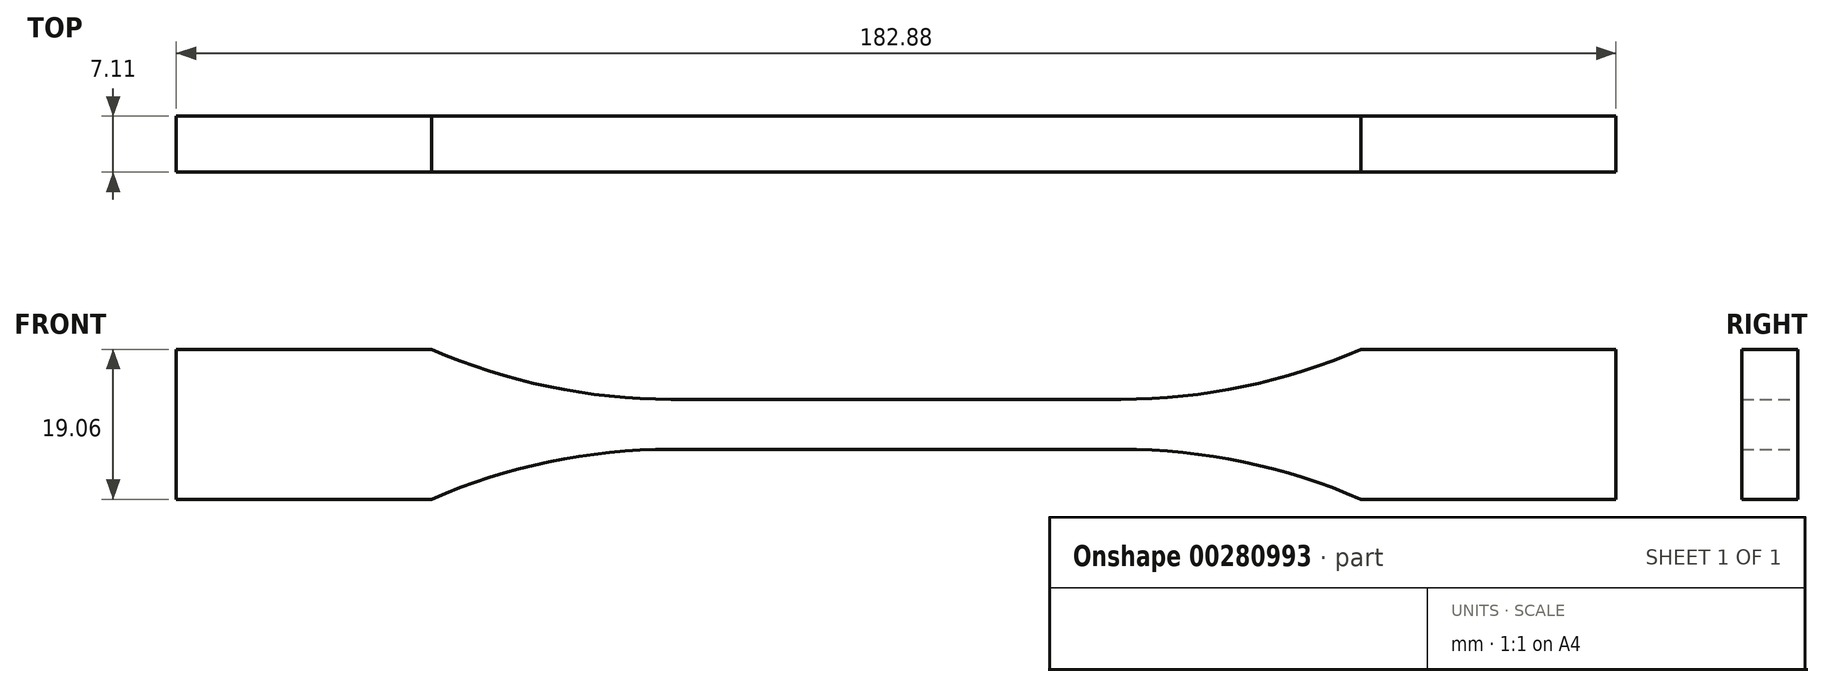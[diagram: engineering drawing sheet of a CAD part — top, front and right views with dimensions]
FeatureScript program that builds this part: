
annotation { "Feature Type Name" : "Feature", "Feature Type Description" : "" }
export const myFeature = defineFeature(function(context is Context, id is Id, definition is map)
    precondition{}
    {
        {
            var Q0;
            Q0=qCreatedBy(makeId("Front.planeOp"),FACE);
            var sketch = newSketch(context, id + "F0", { "sketchPlane" : qUnion([Q0])});
            skLineSegment(sketch, "E0", {"start": v(0, 3.17) * mm, "end": v(28.58, 3.17) * mm});
            skArc(sketch, "E1", {"start": v(28.58, 3.18) * mm, "mid": v(44.13, 4.78) * mm, "end": v(59.03, 9.52) * mm});
            skLineSegment(sketch, "E2", {"start": v(59.03, 9.53) * mm, "end": v(91.44, 9.53) * mm});
            skLineSegment(sketch, "E3", {"start": v(91.44, 9.52) * mm, "end": v(91.44, 0) * mm});
            skLineSegment(sketch, "E4.MirrorCS", {"start": v(59.03, -9.53) * mm, "end": v(91.44, -9.53) * mm});
            skLineSegment(sketch, "E5.MirrorCS", {"start": v(91.44, -9.52) * mm, "end": v(91.44, 0) * mm});
            skLineSegment(sketch, "E6.MirrorCS", {"start": v(0, -3.17) * mm, "end": v(28.58, -3.17) * mm});
            skArc(sketch, "E7.MirrorCS", {"start": v(28.58, -3.18) * mm, "mid": v(44.13, -4.78) * mm, "end": v(59.03, -9.52) * mm});
            skArc(sketch, "E8.MirrorCS", {"start": v(-28.58, -3.18) * mm, "mid": v(-44.13, -4.78) * mm, "end": v(-59.03, -9.52) * mm});
            skLineSegment(sketch, "E9.MirrorCS", {"start": v(0, -3.17) * mm, "end": v(-28.58, -3.17) * mm});
            skArc(sketch, "E10.MirrorCS", {"start": v(-28.58, 3.18) * mm, "mid": v(-44.13, 4.78) * mm, "end": v(-59.03, 9.52) * mm});
            skLineSegment(sketch, "E11.MirrorCS", {"start": v(-59.03, 9.53) * mm, "end": v(-91.44, 9.52) * mm});
            skLineSegment(sketch, "E12.MirrorCS", {"start": v(-91.44, -9.52) * mm, "end": v(-91.44, 0) * mm});
            skLineSegment(sketch, "E13.MirrorCS", {"start": v(-59.03, -9.52) * mm, "end": v(-91.44, -9.52) * mm});
            skLineSegment(sketch, "E14.MirrorCS", {"start": v(-91.44, 9.52) * mm, "end": v(-91.44, 0) * mm});
            skLineSegment(sketch, "E15.MirrorCS", {"start": v(0, 3.18) * mm, "end": v(-28.58, 3.18) * mm});
            skSolve(sketch);
        }
        {
            var Q0;
            Q0 = qSketchRegion(id + "F0", true);
            extrude(context, id + "F1", {"entities" : qUnion([Q0]), "depth" : 7.11 * mm});
        }
    });
